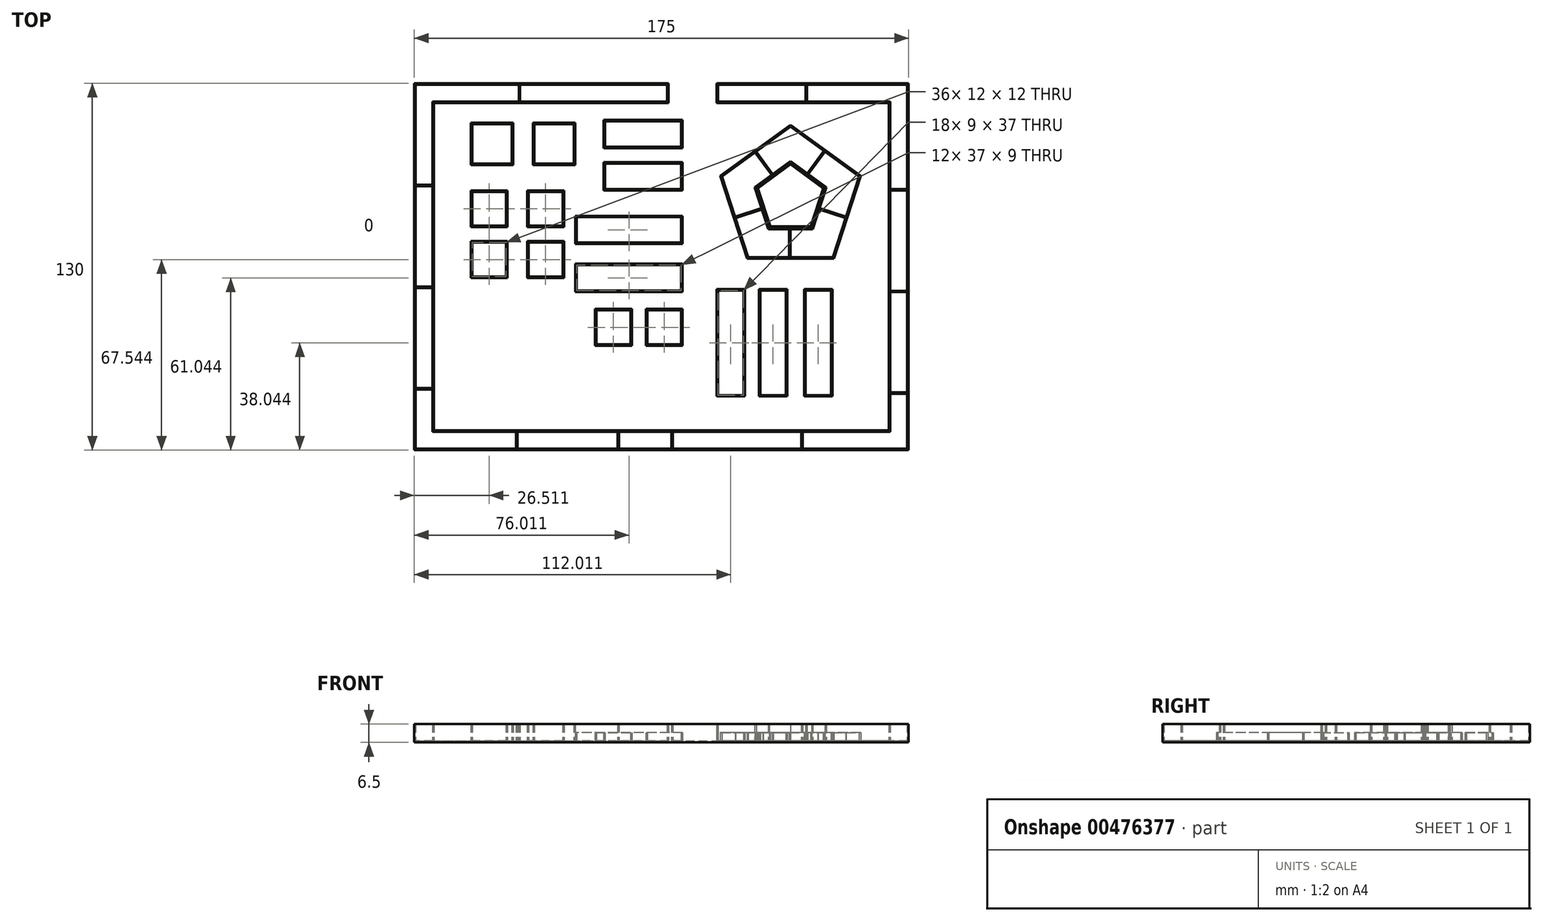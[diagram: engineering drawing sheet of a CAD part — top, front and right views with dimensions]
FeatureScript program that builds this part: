
annotation { "Feature Type Name" : "Feature", "Feature Type Description" : "" }
export const myFeature = defineFeature(function(context is Context, id is Id, definition is map)
    precondition{}
    {
        {
            var Q0;
            Q0=qCreatedBy(makeId("Top.planeOp"),FACE);
            var sketch = newSketch(context, id + "F0", { "sketchPlane" : qUnion([Q0])});
            skLineSegment(sketch, "E0", {"start": v(-85.45, 59.87) * mm, "end": v(-85.45, -69.13) * mm});
            skLineSegment(sketch, "E1.0", {"start": v(88.55, 59.87) * mm, "end": v(88.55, -69.13) * mm});
            skLineSegment(sketch, "E2", {"start": v(-85.45, -69.13) * mm, "end": v(88.55, -69.13) * mm});
            skLineSegment(sketch, "E3", {"start": v(-85.45, 59.87) * mm, "end": v(3.55, 59.87) * mm});
            skLineSegment(sketch, "E4", {"start": v(88.55, 59.87) * mm, "end": v(21.55, 59.87) * mm});
            skLineSegment(sketch, "E5.0", {"start": v(82.93, 53.87) * mm, "end": v(21.55, 53.87) * mm});
            skLineSegment(sketch, "E6.0", {"start": v(82.55, 53.87) * mm, "end": v(82.55, -63.13) * mm});
            skLineSegment(sketch, "E7.0", {"start": v(-79.13, -63.13) * mm, "end": v(82.87, -63.13) * mm});
            skLineSegment(sketch, "E8.0", {"start": v(82.55, 53.87) * mm, "end": v(21.55, 53.87) * mm});
            skLineSegment(sketch, "E8.1", {"start": v(-79.45, 53.87) * mm, "end": v(3.55, 53.87) * mm});
            skLineSegment(sketch, "E8.2", {"start": v(-79.45, 53.87) * mm, "end": v(-79.45, -63.13) * mm});
            skLineSegment(sketch, "E8.3", {"start": v(-79.45, -63.13) * mm, "end": v(82.55, -63.13) * mm});
            skLineSegment(sketch, "E9", {"start": v(3.55, 59.87) * mm, "end": v(3.55, 53.87) * mm});
            skLineSegment(sketch, "E10", {"start": v(21.55, 59.87) * mm, "end": v(21.55, 53.87) * mm});
            skLineSegment(sketch, "E11", {"start": v(-48.45, 59.87) * mm, "end": v(-48.45, 53.87) * mm});
            skLineSegment(sketch, "E12", {"start": v(-48.45, 53.87) * mm, "end": v(3.55, 53.87) * mm});
            skLineSegment(sketch, "E13", {"start": v(-79.45, 23.87) * mm, "end": v(-85.45, 23.87) * mm});
            skLineSegment(sketch, "E14", {"start": v(-85.45, 23.87) * mm, "end": v(-85.45, 59.87) * mm});
            skLineSegment(sketch, "E15", {"start": v(-79.45, -12.13) * mm, "end": v(-85.45, -12.13) * mm});
            skLineSegment(sketch, "E16", {"start": v(-85.45, -12.13) * mm, "end": v(-85.45, 23.87) * mm});
            skLineSegment(sketch, "E17", {"start": v(-79.45, -48.13) * mm, "end": v(-85.45, -48.13) * mm});
            skLineSegment(sketch, "E18", {"start": v(-85.45, -48.13) * mm, "end": v(-85.45, -12.13) * mm});
            skLineSegment(sketch, "E19", {"start": v(-49.45, -63.13) * mm, "end": v(-49.45, -69.13) * mm});
            skLineSegment(sketch, "E20", {"start": v(-49.45, -69.13) * mm, "end": v(-85.45, -69.13) * mm});
            skLineSegment(sketch, "E21", {"start": v(-13.45, -63.13) * mm, "end": v(-13.45, -69.13) * mm});
            skLineSegment(sketch, "E22", {"start": v(-13.45, -69.13) * mm, "end": v(-49.45, -69.13) * mm});
            skLineSegment(sketch, "E23", {"start": v(5.55, -63.13) * mm, "end": v(5.55, -69.13) * mm});
            skLineSegment(sketch, "E24", {"start": v(5.55, -69.13) * mm, "end": v(-13.45, -69.13) * mm});
            skLineSegment(sketch, "E25", {"start": v(51.55, -63.13) * mm, "end": v(51.55, -69.13) * mm});
            skLineSegment(sketch, "E26", {"start": v(51.55, -69.13) * mm, "end": v(5.55, -69.13) * mm});
            skLineSegment(sketch, "E27", {"start": v(82.55, -49.13) * mm, "end": v(88.55, -49.13) * mm});
            skLineSegment(sketch, "E28", {"start": v(88.55, -49.13) * mm, "end": v(88.55, -69.13) * mm});
            skLineSegment(sketch, "E29", {"start": v(82.55, -13.13) * mm, "end": v(88.55, -13.13) * mm});
            skLineSegment(sketch, "E30", {"start": v(88.55, -13.13) * mm, "end": v(88.55, -49.13) * mm});
            skLineSegment(sketch, "E31", {"start": v(82.55, 22.87) * mm, "end": v(88.55, 22.87) * mm});
            skLineSegment(sketch, "E32", {"start": v(88.55, 22.87) * mm, "end": v(88.55, -13.13) * mm});
            skLineSegment(sketch, "E33", {"start": v(52.55, 53.87) * mm, "end": v(52.55, 59.87) * mm});
            skLineSegment(sketch, "E34", {"start": v(52.55, 59.87) * mm, "end": v(88.55, 59.87) * mm});
            skLineSegment(sketch, "E35.0", {"start": v(-48.95, 59.87) * mm, "end": v(-48.95, 53.87) * mm});
            skLineSegment(sketch, "E36.0", {"start": v(-79.45, 24.37) * mm, "end": v(-85.45, 24.37) * mm});
            skLineSegment(sketch, "E37.0", {"start": v(-79.45, -11.63) * mm, "end": v(-85.45, -11.63) * mm});
            skLineSegment(sketch, "E38.0", {"start": v(-79.45, -47.63) * mm, "end": v(-85.45, -47.63) * mm});
            skLineSegment(sketch, "E39.0", {"start": v(-49.95, -63.13) * mm, "end": v(-49.95, -69.13) * mm});
            skLineSegment(sketch, "E40.0", {"start": v(-13.95, -63.13) * mm, "end": v(-13.95, -69.13) * mm});
            skLineSegment(sketch, "E41.0", {"start": v(5.05, -63.13) * mm, "end": v(5.05, -69.13) * mm});
            skLineSegment(sketch, "E42.0", {"start": v(51.05, -63.13) * mm, "end": v(51.05, -69.13) * mm});
            skLineSegment(sketch, "E43.0", {"start": v(82.55, -49.63) * mm, "end": v(88.55, -49.63) * mm});
            skLineSegment(sketch, "E44.0", {"start": v(82.55, -13.63) * mm, "end": v(88.55, -13.63) * mm});
            skLineSegment(sketch, "E45.0", {"start": v(82.55, 22.37) * mm, "end": v(88.55, 22.37) * mm});
            skLineSegment(sketch, "E46.0", {"start": v(53.05, 53.87) * mm, "end": v(53.05, 59.87) * mm});
            skSolve(sketch);
        }
        {
            var Q0;
            Q0=qCreatedBy(makeId("Top.planeOp"),FACE);
            var sketch = newSketch(context, id + "F1", { "sketchPlane" : qUnion([Q0])});
            skLineSegment(sketch, "E47.bottom", {"start": v(52.56, -13.09) * mm, "end": v(61.56, -13.09) * mm});
            skLineSegment(sketch, "E47.top", {"start": v(52.56, -50.09) * mm, "end": v(61.56, -50.09) * mm});
            skLineSegment(sketch, "E47.left", {"start": v(52.56, -13.09) * mm, "end": v(52.56, -50.09) * mm});
            skLineSegment(sketch, "E47.right", {"start": v(61.56, -13.09) * mm, "end": v(61.56, -50.09) * mm});
            skLineSegment(sketch, "E48.bottom", {"start": v(36.56, -13.09) * mm, "end": v(45.56, -13.09) * mm});
            skLineSegment(sketch, "E48.top", {"start": v(36.56, -50.09) * mm, "end": v(45.56, -50.09) * mm});
            skLineSegment(sketch, "E48.left", {"start": v(36.56, -13.09) * mm, "end": v(36.56, -50.09) * mm});
            skLineSegment(sketch, "E48.right", {"start": v(45.56, -13.09) * mm, "end": v(45.56, -50.09) * mm});
            skLineSegment(sketch, "E49.bottom", {"start": v(30.56, -13.09) * mm, "end": v(21.56, -13.09) * mm});
            skLineSegment(sketch, "E49.top", {"start": v(30.56, -50.09) * mm, "end": v(21.56, -50.09) * mm});
            skLineSegment(sketch, "E49.left", {"start": v(30.56, -13.09) * mm, "end": v(30.56, -50.09) * mm});
            skLineSegment(sketch, "E49.right", {"start": v(21.56, -13.09) * mm, "end": v(21.56, -50.09) * mm});
            skLineSegment(sketch, "E50", {"start": v(61.56, -63.09) * mm, "end": v(61.56, -50.09) * mm});
            skLineSegment(sketch, "E51", {"start": v(61.56, -50.09) * mm, "end": v(82.56, -50.09) * mm});
            skLineSegment(sketch, "E52", {"start": v(30.56, -50.09) * mm, "end": v(36.56, -50.09) * mm});
            skLineSegment(sketch, "E53", {"start": v(45.56, -50.09) * mm, "end": v(52.56, -50.09) * mm});
            skLineSegment(sketch, "E54", {"start": v(21.56, -13.09) * mm, "end": v(8.56, -13.09) * mm});
            skLineSegment(sketch, "E55.bottom", {"start": v(8.56, -13.09) * mm, "end": v(-28.44, -13.09) * mm});
            skLineSegment(sketch, "E55.top", {"start": v(8.56, -4.09) * mm, "end": v(-28.44, -4.09) * mm});
            skLineSegment(sketch, "E55.left", {"start": v(8.56, -13.09) * mm, "end": v(8.56, -4.09) * mm});
            skLineSegment(sketch, "E55.right", {"start": v(-28.44, -13.09) * mm, "end": v(-28.44, -4.09) * mm});
            skLineSegment(sketch, "E56.bottom", {"start": v(8.56, 3.91) * mm, "end": v(-28.44, 3.91) * mm});
            skLineSegment(sketch, "E56.top", {"start": v(8.56, 12.91) * mm, "end": v(-28.44, 12.91) * mm});
            skLineSegment(sketch, "E56.left", {"start": v(8.56, 3.91) * mm, "end": v(8.56, 12.91) * mm});
            skLineSegment(sketch, "E56.right", {"start": v(-28.44, 3.91) * mm, "end": v(-28.44, 12.91) * mm});
            skLineSegment(sketch, "E57.bottom", {"start": v(8.56, 22.91) * mm, "end": v(-18.44, 22.91) * mm});
            skLineSegment(sketch, "E57.top", {"start": v(8.56, 31.91) * mm, "end": v(-18.44, 31.91) * mm});
            skLineSegment(sketch, "E57.left", {"start": v(8.56, 22.91) * mm, "end": v(8.56, 31.91) * mm});
            skLineSegment(sketch, "E57.right", {"start": v(-18.44, 22.91) * mm, "end": v(-18.44, 31.91) * mm});
            skLineSegment(sketch, "E58.bottom", {"start": v(8.56, 37.91) * mm, "end": v(-18.44, 37.91) * mm});
            skLineSegment(sketch, "E58.top", {"start": v(8.56, 46.91) * mm, "end": v(-18.44, 46.91) * mm});
            skLineSegment(sketch, "E58.left", {"start": v(8.56, 37.91) * mm, "end": v(8.56, 46.91) * mm});
            skLineSegment(sketch, "E58.right", {"start": v(-18.44, 37.91) * mm, "end": v(-18.44, 46.91) * mm});
            skLineSegment(sketch, "E59.bottom", {"start": v(8.56, -20.09) * mm, "end": v(-3.44, -20.09) * mm});
            skLineSegment(sketch, "E59.top", {"start": v(8.56, -32.09) * mm, "end": v(-3.44, -32.09) * mm});
            skLineSegment(sketch, "E59.left", {"start": v(8.56, -20.09) * mm, "end": v(8.56, -32.09) * mm});
            skLineSegment(sketch, "E59.right", {"start": v(-3.44, -20.09) * mm, "end": v(-3.44, -32.09) * mm});
            skLineSegment(sketch, "E60.bottom", {"start": v(-21.44, -20.09) * mm, "end": v(-9.44, -20.09) * mm});
            skLineSegment(sketch, "E60.top", {"start": v(-21.44, -32.09) * mm, "end": v(-9.44, -32.09) * mm});
            skLineSegment(sketch, "E60.left", {"start": v(-21.44, -20.09) * mm, "end": v(-21.44, -32.09) * mm});
            skLineSegment(sketch, "E60.right", {"start": v(-9.44, -20.09) * mm, "end": v(-9.44, -32.09) * mm});
            skLineSegment(sketch, "E61.bottom", {"start": v(-33.44, -8.09) * mm, "end": v(-45.44, -8.09) * mm});
            skLineSegment(sketch, "E61.top", {"start": v(-33.44, 3.91) * mm, "end": v(-45.44, 3.91) * mm});
            skLineSegment(sketch, "E61.left", {"start": v(-33.44, -8.09) * mm, "end": v(-33.44, 3.91) * mm});
            skLineSegment(sketch, "E61.right", {"start": v(-45.44, -8.09) * mm, "end": v(-45.44, 3.91) * mm});
            skLineSegment(sketch, "E62.bottom", {"start": v(-53.44, -8.09) * mm, "end": v(-65.44, -8.09) * mm});
            skLineSegment(sketch, "E62.top", {"start": v(-53.44, 3.91) * mm, "end": v(-65.44, 3.91) * mm});
            skLineSegment(sketch, "E62.left", {"start": v(-53.44, -8.09) * mm, "end": v(-53.44, 3.91) * mm});
            skLineSegment(sketch, "E62.right", {"start": v(-65.44, -8.09) * mm, "end": v(-65.44, 3.91) * mm});
            skLineSegment(sketch, "E63.bottom", {"start": v(-65.44, 31.91) * mm, "end": v(-51.44, 31.91) * mm});
            skLineSegment(sketch, "E63.top", {"start": v(-65.44, 45.91) * mm, "end": v(-51.44, 45.91) * mm});
            skLineSegment(sketch, "E63.left", {"start": v(-65.44, 31.91) * mm, "end": v(-65.44, 45.91) * mm});
            skLineSegment(sketch, "E63.right", {"start": v(-51.44, 31.91) * mm, "end": v(-51.44, 45.91) * mm});
            skLineSegment(sketch, "E64.bottom", {"start": v(-43.44, 31.91) * mm, "end": v(-29.44, 31.91) * mm});
            skLineSegment(sketch, "E64.top", {"start": v(-43.44, 45.91) * mm, "end": v(-29.44, 45.91) * mm});
            skLineSegment(sketch, "E64.left", {"start": v(-43.44, 31.91) * mm, "end": v(-43.44, 45.91) * mm});
            skLineSegment(sketch, "E64.right", {"start": v(-29.44, 31.91) * mm, "end": v(-29.44, 45.91) * mm});
            skLineSegment(sketch, "E65", {"start": v(8.56, -13.09) * mm, "end": v(8.56, -20.09) * mm});
            skLineSegment(sketch, "E66", {"start": v(-3.44, -32.09) * mm, "end": v(-9.44, -32.09) * mm});
            skLineSegment(sketch, "E67", {"start": v(8.56, -4.09) * mm, "end": v(8.56, 3.91) * mm});
            skLineSegment(sketch, "E68", {"start": v(-33.44, 3.91) * mm, "end": v(-28.44, 3.91) * mm});
            skLineSegment(sketch, "E69", {"start": v(-53.44, 3.91) * mm, "end": v(-45.44, 3.91) * mm});
            skLineSegment(sketch, "E70.bottom", {"start": v(-33.44, 9.91) * mm, "end": v(-45.44, 9.91) * mm});
            skLineSegment(sketch, "E70.top", {"start": v(-33.44, 21.91) * mm, "end": v(-45.44, 21.91) * mm});
            skLineSegment(sketch, "E70.left", {"start": v(-33.44, 9.91) * mm, "end": v(-33.44, 21.91) * mm});
            skLineSegment(sketch, "E70.right", {"start": v(-45.44, 9.91) * mm, "end": v(-45.44, 21.91) * mm});
            skLineSegment(sketch, "E71.bottom", {"start": v(-53.44, 9.91) * mm, "end": v(-65.44, 9.91) * mm});
            skLineSegment(sketch, "E71.top", {"start": v(-53.44, 21.91) * mm, "end": v(-65.44, 21.91) * mm});
            skLineSegment(sketch, "E71.left", {"start": v(-53.44, 9.91) * mm, "end": v(-53.44, 21.91) * mm});
            skLineSegment(sketch, "E71.right", {"start": v(-65.44, 9.91) * mm, "end": v(-65.44, 21.91) * mm});
            skLineSegment(sketch, "E72", {"start": v(-65.44, 21.91) * mm, "end": v(-65.44, 31.91) * mm});
            skLineSegment(sketch, "E73", {"start": v(-51.44, 31.91) * mm, "end": v(-43.44, 31.91) * mm});
            skLineSegment(sketch, "E74", {"start": v(-45.44, 3.91) * mm, "end": v(-45.44, 9.91) * mm});
            skLineSegment(sketch, "E75", {"start": v(8.56, 12.91) * mm, "end": v(8.56, 22.91) * mm});
            skLineSegment(sketch, "E76", {"start": v(8.56, 31.91) * mm, "end": v(8.56, 37.91) * mm});
            skSolve(sketch);
        }
        {
            var Q0;
            Q0=qCreatedBy(makeId("Top.planeOp"),FACE);
            var sketch = newSketch(context, id + "F2", { "sketchPlane" : qUnion([Q0])});
            skLineSegment(sketch, "E77", {"start": v(62.27, -1.2) * mm, "end": v(32.27, -1.2) * mm});
            skLineSegment(sketch, "E78", {"start": v(23, 27.32) * mm, "end": v(32.27, -1.2) * mm});
            skLineSegment(sketch, "E79", {"start": v(62.27, -1.2) * mm, "end": v(71.54, 27.32) * mm});
            skLineSegment(sketch, "E80", {"start": v(71.54, 27.32) * mm, "end": v(47.27, 44.96) * mm});
            skLineSegment(sketch, "E81", {"start": v(47.27, 44.96) * mm, "end": v(23, 27.32) * mm});
            skLineSegment(sketch, "E82", {"start": v(54.77, 9.12) * mm, "end": v(39.77, 9.12) * mm});
            skLineSegment(sketch, "E83", {"start": v(39.77, 9.12) * mm, "end": v(35.13, 23.38) * mm});
            skLineSegment(sketch, "E84", {"start": v(35.13, 23.38) * mm, "end": v(47.27, 32.2) * mm});
            skLineSegment(sketch, "E85", {"start": v(47.27, 32.2) * mm, "end": v(59.4, 23.38) * mm});
            skLineSegment(sketch, "E86", {"start": v(59.4, 23.38) * mm, "end": v(54.77, 9.12) * mm});
            skLineSegment(sketch, "E87", {"start": v(27.63, 13.06) * mm, "end": v(37.45, 16.25) * mm});
            skLineSegment(sketch, "E88", {"start": v(35.13, 36.14) * mm, "end": v(41.2, 27.79) * mm});
            skLineSegment(sketch, "E89", {"start": v(59.4, 36.14) * mm, "end": v(53.34, 27.79) * mm});
            skPoint(sketch, "E89.endSnap0", {"position": v(53.34, 27.79) * mm});
            skLineSegment(sketch, "E90", {"start": v(57.09, 16.25) * mm, "end": v(66.9, 13.06) * mm});
            skLineSegment(sketch, "E91", {"start": v(47.27, 9.12) * mm, "end": v(47.27, -1.2) * mm});
            skLineSegment(sketch, "E92.0", {"start": v(34.73, 35.85) * mm, "end": v(40.8, 27.5) * mm});
            skLineSegment(sketch, "E93.0", {"start": v(59, 36.44) * mm, "end": v(52.93, 28.08) * mm});
            skLineSegment(sketch, "E94.0", {"start": v(56.93, 15.77) * mm, "end": v(66.75, 12.58) * mm});
            skLineSegment(sketch, "E95.0", {"start": v(46.77, 9.12) * mm, "end": v(46.77, -1.2) * mm});
            skLineSegment(sketch, "E96.0", {"start": v(27.79, 12.58) * mm, "end": v(37.6, 15.77) * mm});
            skSolve(sketch);
        }
        {
            var Q0;
            Q0=makeQuery(id+"F1.imprint","IMPRINT",FACE,{"disambiguationData":[TD([[makeQuery(id+"F1.imprint","IMPRINT",EDGE,{"derivedFrom":sQuery(id+"F1.wireOp",EDGE,"E64.bottom")}),1.0]])]});
            var Q1;
            Q1=makeQuery(id+"F1.imprint","IMPRINT",FACE,{"disambiguationData":[TD([[makeQuery(id+"F1.imprint","IMPRINT",EDGE,{"derivedFrom":sQuery(id+"F1.wireOp",EDGE,"E63.bottom")}),1.0]])]});
            var Q2;
            Q2=makeQuery(id+"F1.imprint","IMPRINT",FACE,{"disambiguationData":[TD([[makeQuery(id+"F1.imprint","IMPRINT",EDGE,{"derivedFrom":sQuery(id+"F1.wireOp",EDGE,"E71.bottom")}),-1.0]])]});
            var Q3;
            Q3=makeQuery(id+"F1.imprint","IMPRINT",FACE,{"disambiguationData":[TD([[makeQuery(id+"F1.imprint","IMPRINT",EDGE,{"derivedFrom":sQuery(id+"F1.wireOp",EDGE,"E62.bottom")}),-1.0]])]});
            var Q4;
            Q4=makeQuery(id+"F1.imprint","IMPRINT",FACE,{"disambiguationData":[TD([[makeQuery(id+"F1.imprint","IMPRINT",EDGE,{"derivedFrom":sQuery(id+"F1.wireOp",EDGE,"E61.bottom")}),-1.0]])]});
            var Q5;
            Q5=makeQuery(id+"F1.imprint","IMPRINT",FACE,{"disambiguationData":[TD([[makeQuery(id+"F1.imprint","IMPRINT",EDGE,{"derivedFrom":sQuery(id+"F1.wireOp",EDGE,"E70.bottom")}),-1.0]])]});
            var Q6;
            Q6 = qSketchRegion(id + "F0", true);
            var Q7;
            {var subQ4=sQuery(id+"F2.wireOp",EDGE,"E82");var subQ7=sQuery(id+"F2.wireOp",EDGE,"E86");var subQ8=makeQuery(id+"F2.imprint","INTERSECT",VERTEX,{"derivedFrom":[subQ4,subQ7]});Q7=makeQuery(id+"F2.imprint","IMPRINT",FACE,{"disambiguationData":[TD([[makeQuery(id+"F2.imprint","IMPRINT",EDGE,{"disambiguationData":[TD([[subQ8,-1.0]])],"derivedFrom":subQ4}),-1.0]])]});}
            extrude(context, id + "F3", {"entities" : qUnion([Q0, Q1, Q2, Q3, Q4, Q5, Q6, Q7]), "depth" : 6 * mm});
        }
        {
            var Q0;
            Q0=makeQuery(id+"F3.opExtrude","CAP_FACE",FACE,{"disambiguationData":[OSD([sQuery(id+"F0.wireOp",EDGE,"E0"),sQuery(id+"F0.wireOp",EDGE,"E1.0"),sQuery(id+"F0.wireOp",EDGE,"E2"),sQuery(id+"F0.wireOp",EDGE,"E3"),sQuery(id+"F0.wireOp",EDGE,"E4"),sQuery(id+"F0.wireOp",EDGE,"E8.0"),sQuery(id+"F0.wireOp",EDGE,"E8.1"),sQuery(id+"F0.wireOp",EDGE,"E8.2"),sQuery(id+"F0.wireOp",EDGE,"E8.3"),sQuery(id+"F0.wireOp",EDGE,"E6.0"),sQuery(id+"F0.wireOp",EDGE,"E9"),sQuery(id+"F0.wireOp",EDGE,"E10"),sQuery(id+"F0.wireOp",EDGE,"E12"),sQuery(id+"F0.wireOp",EDGE,"E14"),sQuery(id+"F0.wireOp",EDGE,"E16"),sQuery(id+"F0.wireOp",EDGE,"E18"),sQuery(id+"F0.wireOp",EDGE,"E20"),sQuery(id+"F0.wireOp",EDGE,"E22"),sQuery(id+"F0.wireOp",EDGE,"E24"),sQuery(id+"F0.wireOp",EDGE,"E26"),sQuery(id+"F0.wireOp",EDGE,"E28"),sQuery(id+"F0.wireOp",EDGE,"E30"),sQuery(id+"F0.wireOp",EDGE,"E32"),sQuery(id+"F0.wireOp",EDGE,"E34")])],"isStart":false});
            var Q1;
            Q1=makeQuery(id+"F3.opExtrude","CAP_FACE",FACE,{"disambiguationData":[OSD([sQuery(id+"F1.wireOp",EDGE,"E63.bottom"),sQuery(id+"F1.wireOp",EDGE,"E63.top"),sQuery(id+"F1.wireOp",EDGE,"E63.left"),sQuery(id+"F1.wireOp",EDGE,"E63.right")])],"isStart":false});
            var Q2;
            Q2=makeQuery(id+"F3.opExtrude","CAP_FACE",FACE,{"disambiguationData":[OSD([sQuery(id+"F1.wireOp",EDGE,"E64.bottom"),sQuery(id+"F1.wireOp",EDGE,"E64.top"),sQuery(id+"F1.wireOp",EDGE,"E64.left"),sQuery(id+"F1.wireOp",EDGE,"E64.right")])],"isStart":false});
            var Q3;
            Q3=makeQuery(id+"F3.opExtrude","CAP_FACE",FACE,{"disambiguationData":[OSD([sQuery(id+"F1.wireOp",EDGE,"E70.bottom"),sQuery(id+"F1.wireOp",EDGE,"E70.top"),sQuery(id+"F1.wireOp",EDGE,"E70.left"),sQuery(id+"F1.wireOp",EDGE,"E70.right")])],"isStart":false});
            var Q4;
            Q4=makeQuery(id+"F3.opExtrude","CAP_FACE",FACE,{"disambiguationData":[OSD([sQuery(id+"F1.wireOp",EDGE,"E71.bottom"),sQuery(id+"F1.wireOp",EDGE,"E71.top"),sQuery(id+"F1.wireOp",EDGE,"E71.left"),sQuery(id+"F1.wireOp",EDGE,"E71.right")])],"isStart":false});
            var Q5;
            Q5=makeQuery(id+"F3.opExtrude","CAP_FACE",FACE,{"disambiguationData":[OSD([sQuery(id+"F1.wireOp",EDGE,"E62.bottom"),sQuery(id+"F1.wireOp",EDGE,"E62.top"),sQuery(id+"F1.wireOp",EDGE,"E62.left"),sQuery(id+"F1.wireOp",EDGE,"E62.right")])],"isStart":false});
            var Q6;
            Q6=makeQuery(id+"F3.opExtrude","CAP_FACE",FACE,{"disambiguationData":[OSD([sQuery(id+"F1.wireOp",EDGE,"E61.bottom"),sQuery(id+"F1.wireOp",EDGE,"E61.top"),sQuery(id+"F1.wireOp",EDGE,"E61.left"),sQuery(id+"F1.wireOp",EDGE,"E61.right")])],"isStart":false});
            var Q7;
            Q7=makeQuery(id+"F3.opExtrude","CAP_FACE",FACE,{"disambiguationData":[OSD([sQuery(id+"F1.wireOp",EDGE,"E56.bottom"),sQuery(id+"F1.wireOp",EDGE,"E56.top"),sQuery(id+"F1.wireOp",EDGE,"E56.left"),sQuery(id+"F1.wireOp",EDGE,"E56.right")])],"isStart":false});
            var Q8;
            Q8=makeQuery(id+"F3.opExtrude","CAP_FACE",FACE,{"disambiguationData":[OSD([sQuery(id+"F1.wireOp",EDGE,"E57.bottom"),sQuery(id+"F1.wireOp",EDGE,"E57.top"),sQuery(id+"F1.wireOp",EDGE,"E57.left"),sQuery(id+"F1.wireOp",EDGE,"E57.right")])],"isStart":false});
            var Q9;
            Q9=makeQuery(id+"F3.opExtrude","CAP_FACE",FACE,{"disambiguationData":[OSD([sQuery(id+"F1.wireOp",EDGE,"E58.bottom"),sQuery(id+"F1.wireOp",EDGE,"E58.top"),sQuery(id+"F1.wireOp",EDGE,"E58.left"),sQuery(id+"F1.wireOp",EDGE,"E58.right")])],"isStart":false});
            var Q10;
            Q10=makeQuery(id+"F3.opExtrude","CAP_FACE",FACE,{"disambiguationData":[OSD([sQuery(id+"F2.wireOp",EDGE,"E77"),sQuery(id+"F2.wireOp",EDGE,"E78"),sQuery(id+"F2.wireOp",EDGE,"E79"),sQuery(id+"F2.wireOp",EDGE,"E80"),sQuery(id+"F2.wireOp",EDGE,"E81"),sQuery(id+"F2.wireOp",EDGE,"E82"),sQuery(id+"F2.wireOp",EDGE,"E83"),sQuery(id+"F2.wireOp",EDGE,"E84"),sQuery(id+"F2.wireOp",EDGE,"E85"),sQuery(id+"F2.wireOp",EDGE,"E86")])],"isStart":false});
            var Q11;
            Q11=makeQuery(id+"F3.opExtrude","CAP_FACE",FACE,{"disambiguationData":[OSD([sQuery(id+"F1.wireOp",EDGE,"E49.bottom"),sQuery(id+"F1.wireOp",EDGE,"E49.top"),sQuery(id+"F1.wireOp",EDGE,"E49.left"),sQuery(id+"F1.wireOp",EDGE,"E49.right")])],"isStart":false});
            var Q12;
            Q12=makeQuery(id+"F3.opExtrude","CAP_FACE",FACE,{"disambiguationData":[OSD([sQuery(id+"F1.wireOp",EDGE,"E55.bottom"),sQuery(id+"F1.wireOp",EDGE,"E55.top"),sQuery(id+"F1.wireOp",EDGE,"E55.left"),sQuery(id+"F1.wireOp",EDGE,"E55.right")])],"isStart":false});
            var Q13;
            Q13=makeQuery(id+"F3.opExtrude","CAP_FACE",FACE,{"disambiguationData":[OSD([sQuery(id+"F1.wireOp",EDGE,"E60.bottom"),sQuery(id+"F1.wireOp",EDGE,"E60.top"),sQuery(id+"F1.wireOp",EDGE,"E60.left"),sQuery(id+"F1.wireOp",EDGE,"E60.right")])],"isStart":false});
            var Q14;
            Q14=makeQuery(id+"F3.opExtrude","CAP_FACE",FACE,{"disambiguationData":[OSD([sQuery(id+"F1.wireOp",EDGE,"E59.bottom"),sQuery(id+"F1.wireOp",EDGE,"E59.top"),sQuery(id+"F1.wireOp",EDGE,"E59.left"),sQuery(id+"F1.wireOp",EDGE,"E59.right")])],"isStart":false});
            var Q15;
            Q15=makeQuery(id+"F3.opExtrude","CAP_FACE",FACE,{"disambiguationData":[OSD([sQuery(id+"F1.wireOp",EDGE,"E48.bottom"),sQuery(id+"F1.wireOp",EDGE,"E48.top"),sQuery(id+"F1.wireOp",EDGE,"E48.left"),sQuery(id+"F1.wireOp",EDGE,"E48.right")])],"isStart":false});
            var Q16;
            Q16=makeQuery(id+"F3.opExtrude","CAP_FACE",FACE,{"disambiguationData":[OSD([sQuery(id+"F1.wireOp",EDGE,"E47.bottom"),sQuery(id+"F1.wireOp",EDGE,"E47.top"),sQuery(id+"F1.wireOp",EDGE,"E47.left"),sQuery(id+"F1.wireOp",EDGE,"E47.right")])],"isStart":false});
            shell(context, id + "F4", {"entities" : qUnion([Q0, Q1, Q2, Q3, Q4, Q5, Q6, Q7, Q8, Q9, Q10, Q11, Q12, Q13, Q14, Q15, Q16]), "thickness" : .5 * mm, "oppositeDirection" : true});
        }
        {
            var Q0;
            Q0=makeQuery(id+"F1.imprint","IMPRINT",FACE,{"disambiguationData":[TD([[makeQuery(id+"F1.imprint","IMPRINT",EDGE,{"derivedFrom":sQuery(id+"F1.wireOp",EDGE,"E58.bottom")}),-1.0]])]});
            var Q1;
            Q1=makeQuery(id+"F1.imprint","IMPRINT",FACE,{"disambiguationData":[TD([[makeQuery(id+"F1.imprint","IMPRINT",EDGE,{"derivedFrom":sQuery(id+"F1.wireOp",EDGE,"E57.bottom")}),-1.0]])]});
            var Q2;
            Q2=makeQuery(id+"F1.imprint","IMPRINT",FACE,{"disambiguationData":[TD([[makeQuery(id+"F1.imprint","IMPRINT",EDGE,{"derivedFrom":sQuery(id+"F1.wireOp",EDGE,"E56.bottom")}),-1.0]])]});
            var Q3;
            Q3=makeQuery(id+"F1.imprint","IMPRINT",FACE,{"disambiguationData":[TD([[makeQuery(id+"F1.imprint","IMPRINT",EDGE,{"derivedFrom":sQuery(id+"F1.wireOp",EDGE,"E55.bottom")}),-1.0]])]});
            var Q4;
            Q4=makeQuery(id+"F1.imprint","IMPRINT",FACE,{"disambiguationData":[TD([[makeQuery(id+"F1.imprint","IMPRINT",EDGE,{"derivedFrom":sQuery(id+"F1.wireOp",EDGE,"E60.bottom")}),-1.0]])]});
            var Q5;
            Q5=makeQuery(id+"F1.imprint","IMPRINT",FACE,{"disambiguationData":[TD([[makeQuery(id+"F1.imprint","IMPRINT",EDGE,{"derivedFrom":sQuery(id+"F1.wireOp",EDGE,"E59.bottom")}),1.0]])]});
            var Q6;
            Q6=makeQuery(id+"F1.imprint","IMPRINT",FACE,{"disambiguationData":[TD([[makeQuery(id+"F1.imprint","IMPRINT",EDGE,{"derivedFrom":sQuery(id+"F1.wireOp",EDGE,"E49.bottom")}),1.0]])]});
            var Q7;
            Q7=makeQuery(id+"F1.imprint","IMPRINT",FACE,{"disambiguationData":[TD([[makeQuery(id+"F1.imprint","IMPRINT",EDGE,{"derivedFrom":sQuery(id+"F1.wireOp",EDGE,"E48.bottom")}),-1.0]])]});
            var Q8;
            Q8=makeQuery(id+"F1.imprint","IMPRINT",FACE,{"disambiguationData":[TD([[makeQuery(id+"F1.imprint","IMPRINT",EDGE,{"derivedFrom":sQuery(id+"F1.wireOp",EDGE,"E47.bottom")}),-1.0]])]});
            var Q9;
            {var subQ3=sQuery(id+"F2.wireOp",EDGE,"E87");Q9=makeQuery(id+"F2.imprint","IMPRINT",FACE,{"disambiguationData":[TD([[makeQuery(id+"F2.imprint","IMPRINT",EDGE,{"derivedFrom":subQ3}),1.0]])]});}
            var Q10;
            {var subQ4=sQuery(id+"F2.wireOp",EDGE,"E88");Q10=makeQuery(id+"F2.imprint","IMPRINT",FACE,{"disambiguationData":[TD([[makeQuery(id+"F2.imprint","IMPRINT",EDGE,{"derivedFrom":subQ4}),1.0]])]});}
            var Q11;
            {var subQ4=sQuery(id+"F2.wireOp",EDGE,"E89");Q11=makeQuery(id+"F2.imprint","IMPRINT",FACE,{"disambiguationData":[TD([[makeQuery(id+"F2.imprint","IMPRINT",EDGE,{"derivedFrom":subQ4}),1.0]])]});}
            var Q12;
            {var subQ3=sQuery(id+"F2.wireOp",EDGE,"E90");Q12=makeQuery(id+"F2.imprint","IMPRINT",FACE,{"disambiguationData":[TD([[makeQuery(id+"F2.imprint","IMPRINT",EDGE,{"derivedFrom":subQ3}),-1.0]])]});}
            var Q13;
            {var subQ3=sQuery(id+"F2.wireOp",EDGE,"E87");Q13=makeQuery(id+"F2.imprint","IMPRINT",FACE,{"disambiguationData":[TD([[makeQuery(id+"F2.imprint","IMPRINT",EDGE,{"derivedFrom":subQ3}),-1.0]])]});}
            var Q14;
            {var subQ7=sQuery(id+"F2.wireOp",EDGE,"E95.0");Q14=makeQuery(id+"F2.imprint","IMPRINT",FACE,{"disambiguationData":[TD([[makeQuery(id+"F2.imprint","IMPRINT",EDGE,{"derivedFrom":subQ7}),-1.0]])]});}
            var Q15;
            {var subQ7=sQuery(id+"F2.wireOp",EDGE,"E91");Q15=makeQuery(id+"F2.imprint","IMPRINT",FACE,{"disambiguationData":[TD([[makeQuery(id+"F2.imprint","IMPRINT",EDGE,{"derivedFrom":subQ7}),1.0]])]});}
            var Q16;
            {var subQ0=sQuery(id+"F2.wireOp",EDGE,"E91");Q16=makeQuery(id+"F2.imprint","IMPRINT",FACE,{"disambiguationData":[TD([[makeQuery(id+"F2.imprint","IMPRINT",EDGE,{"derivedFrom":subQ0}),-1.0]])]});}
            var Q17;
            {var subQ0=sQuery(id+"F2.wireOp",EDGE,"E89");Q17=makeQuery(id+"F2.imprint","IMPRINT",FACE,{"disambiguationData":[TD([[makeQuery(id+"F2.imprint","IMPRINT",EDGE,{"derivedFrom":subQ0}),-1.0]])]});}
            var Q18;
            {var subQ0=sQuery(id+"F2.wireOp",EDGE,"E88");Q18=makeQuery(id+"F2.imprint","IMPRINT",FACE,{"disambiguationData":[TD([[makeQuery(id+"F2.imprint","IMPRINT",EDGE,{"derivedFrom":subQ0}),-1.0]])]});}
            extrude(context, id + "F5", {"entities" : qUnion([Q0, Q1, Q2, Q3, Q4, Q5, Q6, Q7, Q8, Q9, Q10, Q11, Q12, Q13, Q14, Q15, Q16, Q17, Q18]), "depth" : 3 * mm});
        }
        {
            var Q0;
            Q0=makeQuery(id+"F5.opExtrude","CAP_FACE",FACE,{"disambiguationData":[OSD([sQuery(id+"F1.wireOp",EDGE,"E58.bottom"),sQuery(id+"F1.wireOp",EDGE,"E58.top"),sQuery(id+"F1.wireOp",EDGE,"E58.left"),sQuery(id+"F1.wireOp",EDGE,"E58.right")])],"isStart":false});
            var Q1;
            Q1=makeQuery(id+"F5.opExtrude","CAP_FACE",FACE,{"disambiguationData":[OSD([sQuery(id+"F1.wireOp",EDGE,"E57.bottom"),sQuery(id+"F1.wireOp",EDGE,"E57.top"),sQuery(id+"F1.wireOp",EDGE,"E57.left"),sQuery(id+"F1.wireOp",EDGE,"E57.right")])],"isStart":false});
            var Q2;
            Q2=makeQuery(id+"F5.opExtrude","CAP_FACE",FACE,{"disambiguationData":[OSD([sQuery(id+"F1.wireOp",EDGE,"E56.bottom"),sQuery(id+"F1.wireOp",EDGE,"E56.top"),sQuery(id+"F1.wireOp",EDGE,"E56.left"),sQuery(id+"F1.wireOp",EDGE,"E56.right")])],"isStart":false});
            var Q3;
            Q3=makeQuery(id+"F5.opExtrude","CAP_FACE",FACE,{"disambiguationData":[OSD([sQuery(id+"F1.wireOp",EDGE,"E55.bottom"),sQuery(id+"F1.wireOp",EDGE,"E55.top"),sQuery(id+"F1.wireOp",EDGE,"E55.left"),sQuery(id+"F1.wireOp",EDGE,"E55.right")])],"isStart":false});
            var Q4;
            Q4=makeQuery(id+"F5.opExtrude","CAP_FACE",FACE,{"disambiguationData":[OSD([sQuery(id+"F1.wireOp",EDGE,"E60.bottom"),sQuery(id+"F1.wireOp",EDGE,"E60.top"),sQuery(id+"F1.wireOp",EDGE,"E60.left"),sQuery(id+"F1.wireOp",EDGE,"E60.right")])],"isStart":false});
            var Q5;
            Q5=makeQuery(id+"F5.opExtrude","CAP_FACE",FACE,{"disambiguationData":[OSD([sQuery(id+"F1.wireOp",EDGE,"E59.bottom"),sQuery(id+"F1.wireOp",EDGE,"E59.top"),sQuery(id+"F1.wireOp",EDGE,"E59.left"),sQuery(id+"F1.wireOp",EDGE,"E59.right")])],"isStart":false});
            var Q6;
            Q6=makeQuery(id+"F5.opExtrude","CAP_FACE",FACE,{"disambiguationData":[OSD([sQuery(id+"F1.wireOp",EDGE,"E49.bottom"),sQuery(id+"F1.wireOp",EDGE,"E49.top"),sQuery(id+"F1.wireOp",EDGE,"E49.left"),sQuery(id+"F1.wireOp",EDGE,"E49.right")])],"isStart":false});
            var Q7;
            Q7=makeQuery(id+"F5.opExtrude","CAP_FACE",FACE,{"disambiguationData":[OSD([sQuery(id+"F1.wireOp",EDGE,"E48.bottom"),sQuery(id+"F1.wireOp",EDGE,"E48.top"),sQuery(id+"F1.wireOp",EDGE,"E48.left"),sQuery(id+"F1.wireOp",EDGE,"E48.right")])],"isStart":false});
            var Q8;
            Q8=makeQuery(id+"F5.opExtrude","CAP_FACE",FACE,{"disambiguationData":[OSD([sQuery(id+"F1.wireOp",EDGE,"E47.bottom"),sQuery(id+"F1.wireOp",EDGE,"E47.top"),sQuery(id+"F1.wireOp",EDGE,"E47.left"),sQuery(id+"F1.wireOp",EDGE,"E47.right")])],"isStart":false});
            var Q9;
            Q9=makeQuery(id+"F5.opExtrude","CAP_FACE",FACE,{"disambiguationData":[OSD([sQuery(id+"F2.wireOp",EDGE,"E77"),sQuery(id+"F2.wireOp",EDGE,"E78"),sQuery(id+"F2.wireOp",EDGE,"E79"),sQuery(id+"F2.wireOp",EDGE,"E80"),sQuery(id+"F2.wireOp",EDGE,"E81"),sQuery(id+"F2.wireOp",EDGE,"E82"),sQuery(id+"F2.wireOp",EDGE,"E83"),sQuery(id+"F2.wireOp",EDGE,"E84"),sQuery(id+"F2.wireOp",EDGE,"E85"),sQuery(id+"F2.wireOp",EDGE,"E86")])],"isStart":false});
            shell(context, id + "F6", {"entities" : qUnion([Q0, Q1, Q2, Q3, Q4, Q5, Q6, Q7, Q8, Q9]), "thickness" : .5 * mm, "oppositeDirection" : true});
        }
        {
            var Q0;
            {var subQ0=sQuery(id+"F0.wireOp",EDGE,"E11");Q0=makeQuery(id+"F0.imprint","IMPRINT",FACE,{"disambiguationData":[TD([[makeQuery(id+"F0.imprint","IMPRINT",EDGE,{"derivedFrom":subQ0}),-1.0]])]});}
            var Q1;
            {var subQ0=sQuery(id+"F0.wireOp",EDGE,"E13");Q1=makeQuery(id+"F0.imprint","IMPRINT",FACE,{"disambiguationData":[TD([[makeQuery(id+"F0.imprint","IMPRINT",EDGE,{"derivedFrom":subQ0}),-1.0]])]});}
            var Q2;
            {var subQ0=sQuery(id+"F0.wireOp",EDGE,"E15");Q2=makeQuery(id+"F0.imprint","IMPRINT",FACE,{"disambiguationData":[TD([[makeQuery(id+"F0.imprint","IMPRINT",EDGE,{"derivedFrom":subQ0}),-1.0]])]});}
            var Q3;
            {var subQ0=sQuery(id+"F0.wireOp",EDGE,"E17");Q3=makeQuery(id+"F0.imprint","IMPRINT",FACE,{"disambiguationData":[TD([[makeQuery(id+"F0.imprint","IMPRINT",EDGE,{"derivedFrom":subQ0}),-1.0]])]});}
            var Q4;
            {var subQ0=sQuery(id+"F0.wireOp",EDGE,"E19");Q4=makeQuery(id+"F0.imprint","IMPRINT",FACE,{"disambiguationData":[TD([[makeQuery(id+"F0.imprint","IMPRINT",EDGE,{"derivedFrom":subQ0}),-1.0]])]});}
            var Q5;
            {var subQ0=sQuery(id+"F0.wireOp",EDGE,"E21");Q5=makeQuery(id+"F0.imprint","IMPRINT",FACE,{"disambiguationData":[TD([[makeQuery(id+"F0.imprint","IMPRINT",EDGE,{"derivedFrom":subQ0}),-1.0]])]});}
            var Q6;
            {var subQ0=sQuery(id+"F0.wireOp",EDGE,"E23");Q6=makeQuery(id+"F0.imprint","IMPRINT",FACE,{"disambiguationData":[TD([[makeQuery(id+"F0.imprint","IMPRINT",EDGE,{"derivedFrom":subQ0}),-1.0]])]});}
            var Q7;
            {var subQ0=sQuery(id+"F0.wireOp",EDGE,"E25");Q7=makeQuery(id+"F0.imprint","IMPRINT",FACE,{"disambiguationData":[TD([[makeQuery(id+"F0.imprint","IMPRINT",EDGE,{"derivedFrom":subQ0}),-1.0]])]});}
            var Q8;
            {var subQ0=sQuery(id+"F0.wireOp",EDGE,"E27");Q8=makeQuery(id+"F0.imprint","IMPRINT",FACE,{"disambiguationData":[TD([[makeQuery(id+"F0.imprint","IMPRINT",EDGE,{"derivedFrom":subQ0}),-1.0]])]});}
            var Q9;
            {var subQ0=sQuery(id+"F0.wireOp",EDGE,"E29");Q9=makeQuery(id+"F0.imprint","IMPRINT",FACE,{"disambiguationData":[TD([[makeQuery(id+"F0.imprint","IMPRINT",EDGE,{"derivedFrom":subQ0}),-1.0]])]});}
            var Q10;
            {var subQ0=sQuery(id+"F0.wireOp",EDGE,"E31");Q10=makeQuery(id+"F0.imprint","IMPRINT",FACE,{"disambiguationData":[TD([[makeQuery(id+"F0.imprint","IMPRINT",EDGE,{"derivedFrom":subQ0}),-1.0]])]});}
            var Q11;
            {var subQ0=sQuery(id+"F0.wireOp",EDGE,"E33");Q11=makeQuery(id+"F0.imprint","IMPRINT",FACE,{"disambiguationData":[TD([[makeQuery(id+"F0.imprint","IMPRINT",EDGE,{"derivedFrom":subQ0}),-1.0]])]});}
            extrude(context, id + "F7", {"entities" : qUnion([Q0, Q1, Q2, Q3, Q4, Q5, Q6, Q7, Q8, Q9, Q10, Q11]), "operationType" : NewBodyOperationType.ADD, "depth" : 6 * mm});
        }
        {
            var Q0;
            {var subQ0=sQuery(id+"F2.wireOp",EDGE,"E87");Q0=makeQuery(id+"F2.imprint","IMPRINT",FACE,{"disambiguationData":[TD([[makeQuery(id+"F2.imprint","IMPRINT",EDGE,{"derivedFrom":subQ0}),-1.0]])]});}
            var Q1;
            {var subQ0=sQuery(id+"F2.wireOp",EDGE,"E91");Q1=makeQuery(id+"F2.imprint","IMPRINT",FACE,{"disambiguationData":[TD([[makeQuery(id+"F2.imprint","IMPRINT",EDGE,{"derivedFrom":subQ0}),-1.0]])]});}
            var Q2;
            {var subQ0=sQuery(id+"F2.wireOp",EDGE,"E90");Q2=makeQuery(id+"F2.imprint","IMPRINT",FACE,{"disambiguationData":[TD([[makeQuery(id+"F2.imprint","IMPRINT",EDGE,{"derivedFrom":subQ0}),-1.0]])]});}
            var Q3;
            {var subQ0=sQuery(id+"F2.wireOp",EDGE,"E89");Q3=makeQuery(id+"F2.imprint","IMPRINT",FACE,{"disambiguationData":[TD([[makeQuery(id+"F2.imprint","IMPRINT",EDGE,{"derivedFrom":subQ0}),-1.0]])]});}
            var Q4;
            {var subQ0=sQuery(id+"F2.wireOp",EDGE,"E88");Q4=makeQuery(id+"F2.imprint","IMPRINT",FACE,{"disambiguationData":[TD([[makeQuery(id+"F2.imprint","IMPRINT",EDGE,{"derivedFrom":subQ0}),-1.0]])]});}
            extrude(context, id + "F8", {"entities" : qUnion([Q0, Q1, Q2, Q3, Q4]), "depth" : 3 * mm});
        }
    });
